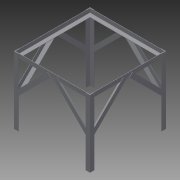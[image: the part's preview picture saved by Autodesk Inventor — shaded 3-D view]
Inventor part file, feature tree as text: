
AUTODESK INVENTOR PART (.ipt)
format: ipt  version: 2014 (Build 180170000, 170)  size: 222,208 bytes
history: native  units: in
note: dims shown in document units (in); Inventor stores cm internally (conversion verified against a paired STEP export)
features: extrude x7, sketch x4, mirror x2, projected_geometry x1
ambient origin geometry x8: Origin, YZ Plane, XZ Plane, XY Plane, X Axis, Y Axis, Z Axis, Center Point
bodies: Solid1 (feature_tree)
feature tree (14):
  sketch  "Sketch1"  dims[d0=26.25in d1=26.25in]
  extrude  "Extrusion1"  Depth=26.25in
  extrude  "Extrusion2"  Depth=0.125in
  sketch  "Sketch2"  dims[d4=0.125in d5=0.125in]
  extrude  "Extrusion3"  Depth=1.375in TaperAngle=0.0deg
  sketch  "Sketch4"  dims[d6=0.125in d7=0.0in d8=1.375in d9=0.0in]
  extrude  "Extrusion5"  Depth=0.125in
  extrude  "Extrusion6"  Depth=23.6875in TaperAngle=0.0deg
  sketch  "Sketch5"  dims[d10=0.125in d15=0.125in d17=23.6875in d18=0.0in d23=1.5in d28=0.125in d29=1.375in d30=0.0in d31=0.125in d32=0.0in d33=1.5in d35=0.125in d37=0.125in d38=0.0in d39=1.5in d40=0.0in d45=45.0deg d47=45.0deg d48=16.0in d49=16.0in d50=1.5in d51=1.5in d52=1.5in d53=1.5in]
  extrude  "Extrusion7"  Depth=1.5in
  extrude  "Extrusion8"  Depth=0.125in
  mirror  "Mirror1"
  mirror  "Mirror2"
  projected_geometry  "Projected Loop1"
